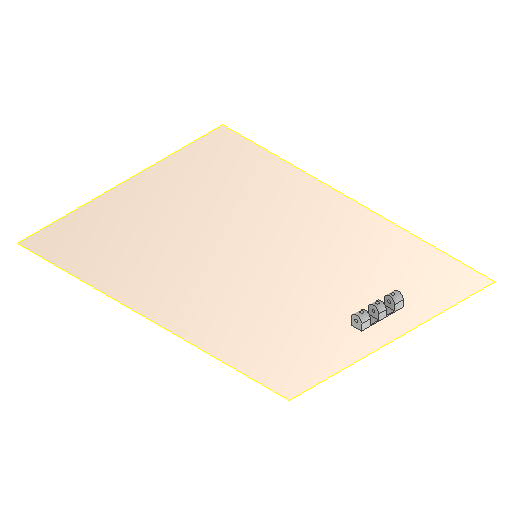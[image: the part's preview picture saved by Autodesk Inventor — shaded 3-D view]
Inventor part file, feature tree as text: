
AUTODESK INVENTOR PART (.ipt)
format: ipt  version: 2024.1 (Build 281209000, 209)  size: 186,368 bytes
history: native  units: mm
features: extrude x3, sketch x3, other x2, plane x1, fillet x1, reference x1, projected_geometry x1
ambient origin geometry x8: Origin, YZ Plane, XZ Plane, XY Plane, X Axis, Y Axis, Z Axis, Center Point
bodies: Volumenkörper1 (feature_tree)
feature tree (12):
  plane  "Arbeitsebene1"
  extrude  "Extrusion1"  Depth=10.0mm
  fillet  "Rundung1"  Radius=50.0mm
  extrude  "Extrusion2"  Depth=5.0mm
  extrude  "Extrusion3"  Depth=10.0mm
  sketch  "Skizze1"  dims[d0=10.0mm d1=40.0mm d2=50.0mm d3=0.0mm]
  reference  "Referenz1"
  sketch  "Skizze2"  dims[d4=5.0mm d5=6.0mm]
  projected_geometry  "Projizierte Kontur1"
  sketch  "Skizze3"  dims[d6=0.0mm d7=0.0mm d8=2.8mm d9=10.0mm d10=8.0mm d11=10.0mm d12=8.0mm d13=2.0mm d14=2.2mm d15=10.0mm d16=0.0mm]
  other  "Assembly_Planktoscope_Uc2version_wormdrive_V3.iam"
  other  "60_Planktoscope_MicroscopeHolder_Bottom_v0:1"
